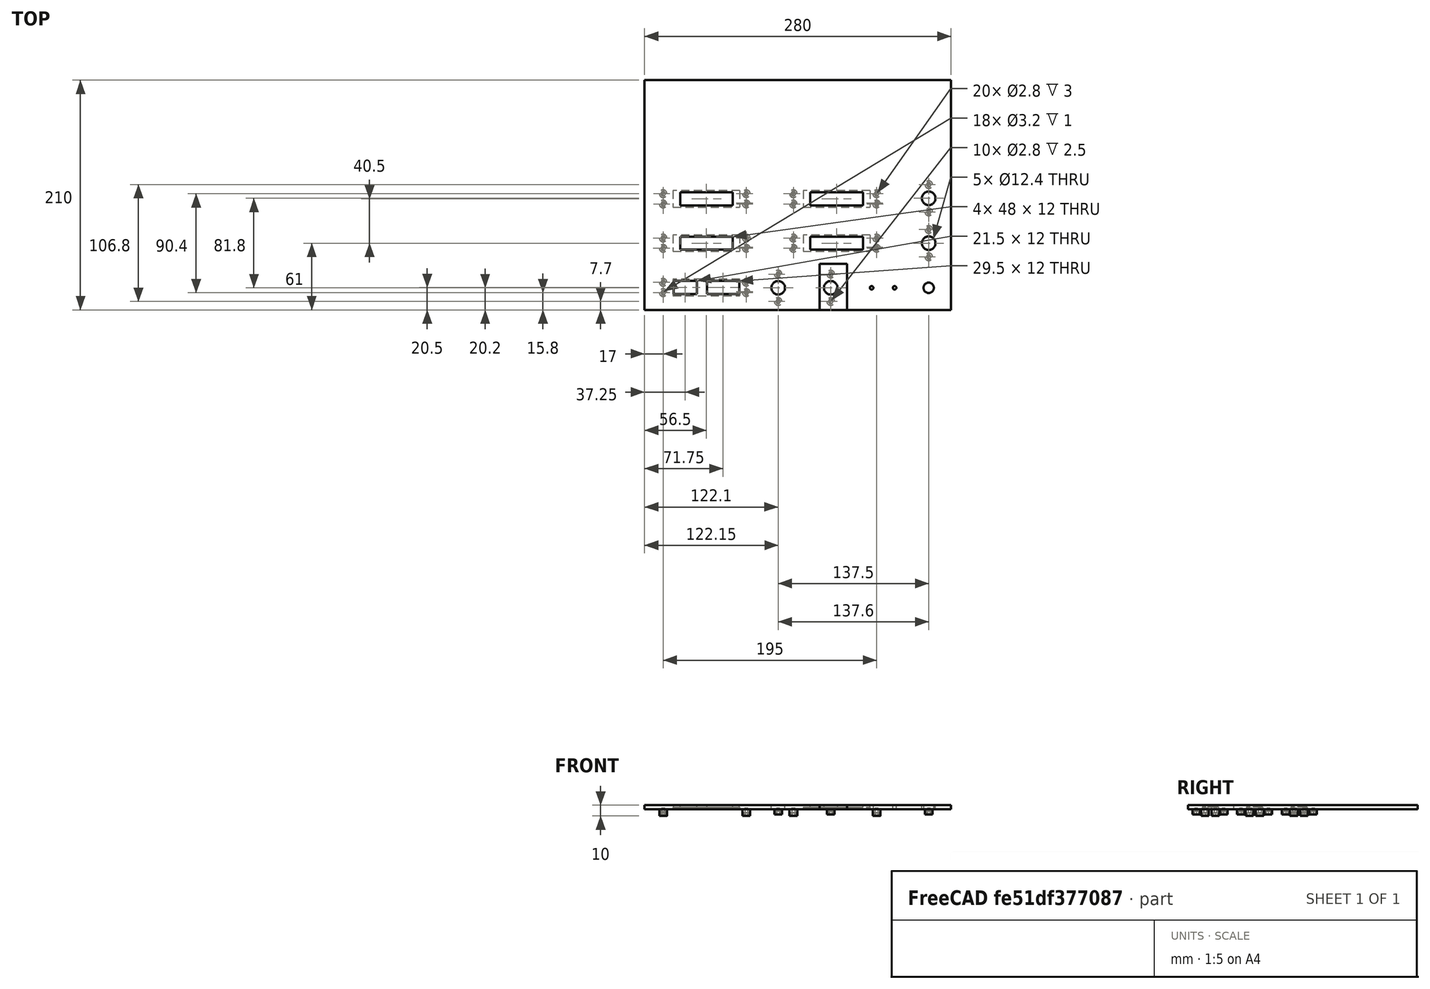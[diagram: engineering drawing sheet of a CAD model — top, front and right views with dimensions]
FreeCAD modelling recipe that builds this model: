
FCSTD DOCUMENT  (FreeCAD 0.17R13522 (Git))
Label: test_panel_para_encoder_doble
License: CreativeCommons Attribution-ShareAlike
LicenseURL: http://creativecommons.org/licenses/by-sa/4.0/
objects: Part::Feature×69, Part::Fuse×58, Part::Cut×20, Part::Box×8, Part::Part2DObjectPython×8, Part::FeaturePython×4, App::DocumentObjectGroup×2, Part::Extrusion×1
note: 168 computed .brp shape members not serialized (recipe doc carries the construction recipe); baked Part::Feature solids carry a one-line shape summary decoded from their .brp

FEATURE [Part::Box] Box  label="base principal"
  AttacherType = Attacher::AttachEngine3D
  Height = 4
  Length = 280
  Placement = pos=(0,0,-4) rot=(0,0,1;0rad)
  Width = 210
FEATURE [Part::Feature] Fusion008001001  label="perforador encoder"
  Placement = pos=(17,17,-6) rot=(1,0,0;3.14159rad)
  shape: bbox 82.5 x 15 x 10 mm, 18 faces (baked)
FEATURE [Part::Feature] Fusion008001001001  label="perforador active 1"
  Placement = pos=(17,98,-6) rot=(1,0,0;3.14159rad)
  shape: bbox 82.5 x 15 x 10 mm, 18 faces (baked)
FEATURE [Part::Feature] Fusion008001001002  label="perforador active 2"
  Placement = pos=(17,57.5,-6) rot=(1,0,0;3.14159rad)
  shape: bbox 82.5 x 15 x 10 mm, 18 faces (baked)
FEATURE [Part::Feature] Fusion008001001003  label="perforador standby 1"
  Placement = pos=(136,98,-6) rot=(1,0,0;3.14159rad)
  shape: bbox 82.5 x 15 x 10 mm, 18 faces (baked)
FEATURE [Part::Feature] Fusion008001001004  label="perforador standby 2"
  Placement = pos=(136,57.5,-6) rot=(1,0,0;3.14159rad)
  shape: bbox 82.5 x 15 x 10 mm, 18 faces (baked)
FEATURE [Part::Cut] Cut
  Base = -> Box
  Refine = true
  Tool = -> Fusion008001001
FEATURE [Part::Cut] Cut001
  Base = -> Cut
  Refine = true
  Tool = -> Fusion008001001001
FEATURE [Part::Cut] Cut002
  Base = -> Cut001
  Refine = true
  Tool = -> Fusion008001001002
FEATURE [Part::Cut] Cut003
  Base = -> Cut002
  Refine = true
  Tool = -> Fusion008001001003
FEATURE [Part::Cut] Cut004  label="base con 7 segmentos sin frente perforado"
  Base = -> Cut003
  Refine = true
  Tool = -> Fusion008001001004
FEATURE [Part::Feature] BooleanFragments001  label="perforador encoder izquierda"
  Placement = pos=(130,20.2,4) rot=(0,0,1;0rad)
  shape: bbox 45.2 x 30 x 10 mm, 34 faces, 4 solids (baked)
FEATURE [Part::Feature] BooleanFragments002  label="perforador encoder derecha"
  Placement = pos=(178,20.2,4) rot=(0,0,1;0rad)
  shape: bbox 45.2 x 30 x 10 mm, 34 faces, 4 solids (baked)
FEATURE [Part::Cut] Cut005
  Base = -> Cut004
  Refine = true
  Tool = -> BooleanFragments001
FEATURE [Part::Cut] Cut006  label="frente con agujeros displays y encoders transponder"
  Base = -> Cut005
  Refine = true
  Tool = -> BooleanFragments002
FEATURE [Part::Feature] Fusion005001  label="boton ident"
  Placement = pos=(203,14.2,1) rot=(0,0,1;0rad)
  shape: bbox 30 x 12 x 10 mm, 14 faces (baked)
FEATURE [Part::Cut] Cut007
  Base = -> Cut006
  Refine = true
  Tool = -> Fusion005001
FEATURE [Part::Part2DObjectPython] Line009  # Draft 2D object (typed FeaturePython)
  ChamferSize = 0
  Closed = false
  End = (270.847,20.2,0)
  FilletRadius = 0
  Length = 35.3471
  MakeFace = false
  Points = (2) [(235.5,20.2,0),(270.847,20.2,0)]
  Start = (235.5,20.2,0)
  Subdivisions = 0
FEATURE [Part::Part2DObjectPython] Circle  # Draft 2D object (typed FeaturePython)
  FirstAngle = 0
  LastAngle = 0
  MakeFace = false
  Placement = pos=(269.619,20.2,4) rot=(0,0,1;0rad)
  Radius = 4.75
FEATURE [Part::Part2DObjectPython] Circle001  # Draft 2D object (typed FeaturePython)
  FirstAngle = 0
  LastAngle = 0
  MakeFace = false
  Placement = pos=(259.67,20.2,0) rot=(0,0,1;0rad)
  Radius = 14
FEATURE [Part::Extrusion] Extrude
  Base = -> Circle
  Dir = (0,0,1)
  DirMode = 2
  FaceMakerClass = Part::FaceMakerBullseye
  LengthFwd = 10
  LengthRev = 0
  Placement = pos=(-10,0,-10) rot=(0,0,1;0rad)
  Solid = true
  Symmetric = false
FEATURE [Part::Part2DObjectPython] Line014  # Draft 2D object (typed FeaturePython)
  ChamferSize = 0
  Closed = false
  End = (248.272,28.2144,0)
  FilletRadius = 0
  Length = 13.696
  MakeFace = false
  Placement = pos=(-10,0,-4) rot=(0,0,1;0rad)
  Points = (2) [(269.378,20.2,4),(258.272,28.2144,4)]
  Start = (259.378,20.2,0)
  Subdivisions = 0
FEATURE [Part::Part2DObjectPython] Line015  # Draft 2D object (typed FeaturePython)
  ChamferSize = 0
  Closed = false
  End = (254.876,33.263,0)
  FilletRadius = 0
  Length = 13.7518
  MakeFace = false
  Placement = pos=(-10,0,-4) rot=(0,0,1;0rad)
  Points = (2) [(269.174,20.2,4),(264.876,33.263,4)]
  Start = (259.174,20.2,0)
  Subdivisions = 0
FEATURE [Part::Part2DObjectPython] Line016  # Draft 2D object (typed FeaturePython)
  ChamferSize = 0
  Closed = false
  End = (263.227,33.6931,0)
  FilletRadius = 0
  Length = 14.1488
  MakeFace = false
  Placement = pos=(-10,0,-4) rot=(0,0,1;0rad)
  Points = (2) [(268.97,20.2,4),(273.227,33.6931,4)]
  Start = (258.97,20.2,0)
  Subdivisions = 0
FEATURE [Part::Part2DObjectPython] Line017  # Draft 2D object (typed FeaturePython)
  ChamferSize = 0
  Closed = false
  End = (270.612,28.9289,0)
  FilletRadius = 0
  Length = 14.5511
  MakeFace = false
  Placement = pos=(-10,0,-4) rot=(0,0,1;0rad)
  Points = (2) [(268.97,20.2,4),(280.612,28.9289,4)]
  Start = (258.97,20.2,0)
  Subdivisions = 0
FEATURE [Part::Part2DObjectPython] Line  # Draft 2D object (typed FeaturePython)
  ChamferSize = 0
  Closed = true
  End = (269.619,20.2,0)
  FilletRadius = 0
  Length = 0
  MakeFace = false
  Points = (2) [(269.619,20.2,0),(269.619,20.2,0)]
  Start = (269.619,20.2,0)
  Subdivisions = 0
FEATURE [App::DocumentObjectGroup] Construction
  Group = -> [Line009,Circle001,Line014,Line015,Line016,Line017,Line]
FEATURE [Part::Cut] Cut008  label="base con line inferior completa"
  Base = -> Cut007
  Refine = true
  Tool = -> Extrude
FEATURE [Part::Feature] BooleanFragments003  label="perforador para comunication 1"
  Placement = pos=(251.8,102,3) rot=(0,0,1;3.14159rad)
  shape: bbox 45.2 x 30 x 10 mm, 34 faces, 4 solids (baked)
FEATURE [Part::Feature] BooleanFragments003001  label="perforador para comunication 2"
  Placement = pos=(251.8,61,4) rot=(0,0,1;3.14159rad)
  shape: bbox 45.2 x 30 x 10 mm, 34 faces, 4 solids (baked)
FEATURE [Part::Cut] Cut009
  Base = -> Cut008
  Refine = true
  Tool = -> BooleanFragments003001
FEATURE [Part::Cut] Cut010  label="panel sin botones y sin leds"
  Base = -> Cut009
  Refine = true
  Tool = -> BooleanFragments003
FEATURE [Part::Feature] Cut001001  label="the_spacer_1mm_inside"
  Placement = pos=(17,106.2,0) rot=(0.99953,0.030644,0;3.14159rad)
  shape: bbox 7 x 7 x 6 mm, 11 faces (baked)
FEATURE [Part::Fuse] Fusion
  Base = -> Cut010
  Refine = true
  Tool = -> Cut001001
FEATURE [Part::Box] Box001  label="Cube"
  AttacherType = Attacher::AttachEngine3D
  Height = 3
  Length = 6
  Placement = pos=(14,103,-3) rot=(0,0,1;0rad)
  Width = 6
FEATURE [Part::Fuse] Fusion008001001005
  Base = -> Fusion
  Refine = true
  Tool = -> Box001
FEATURE [Part::Feature] Cut001001001  label="the_spacer_1mm_inside001"
  Placement = pos=(17,96.8,0) rot=(0.99953,0.030644,0;3.14159rad)
  shape: bbox 7 x 7 x 6 mm, 11 faces (baked)
FEATURE [Part::Feature] Box001001  label="Cube001"
  Placement = pos=(14,94,-3) rot=(0,0,1;0rad)
  shape: bbox 6 x 6 x 3 mm, 6 faces (baked)
FEATURE [Part::Fuse] Fusion008001001006
  Base = -> Fusion008001001005
  Refine = true
  Tool = -> Cut001001001
FEATURE [Part::Fuse] Fusion008001001007
  Base = -> Box001001
  Placement = pos=(0,0,1) rot=(0,0,1;0rad)
  Refine = true
  Tool = -> Fusion008001001006
FEATURE [Part::Feature] Cut001001001001  label="the_spacer_1mm_inside002"
  Placement = pos=(17,56.3,0) rot=(0.99953,0.030644,0;3.14159rad)
  shape: bbox 7 x 7 x 6 mm, 11 faces (baked)
FEATURE [Part::Feature] Cut001001001002  label="the_spacer_1mm_inside003"
  Placement = pos=(17,65.7,0) rot=(0.99953,0.030644,0;3.14159rad)
  shape: bbox 7 x 7 x 6 mm, 11 faces (baked)
FEATURE [Part::Feature] Cut001001001002001  label="the_spacer_1mm_inside004"
  Placement = pos=(17,25.2,0) rot=(0.99953,0.030644,0;3.14159rad)
  shape: bbox 7 x 7 x 6 mm, 11 faces (baked)
FEATURE [Part::Feature] Cut001001001001001  label="the_spacer_1mm_inside005"
  Placement = pos=(17,15.8,0) rot=(0.99953,0.030644,0;3.14159rad)
  shape: bbox 7 x 7 x 6 mm, 11 faces (baked)
FEATURE [Part::Feature] Cut001001001002002  label="the_spacer_1mm_inside006"
  Placement = pos=(136,106.2,0) rot=(0.99953,0.030644,0;3.14159rad)
  shape: bbox 7 x 7 x 6 mm, 11 faces (baked)
FEATURE [Part::Feature] Cut001001001002003  label="the_spacer_1mm_inside007"
  Placement = pos=(136,96.8,0) rot=(0.99953,0.030644,0;3.14159rad)
  shape: bbox 7 x 7 x 6 mm, 11 faces (baked)
FEATURE [Part::Feature] Cut001001001002004  label="the_spacer_1mm_inside008"
  Placement = pos=(136,65.7,0) rot=(0.99953,0.030644,0;3.14159rad)
  shape: bbox 7 x 7 x 6 mm, 11 faces (baked)
FEATURE [Part::Feature] Cut001001001001002  label="the_spacer_1mm_inside009"
  Placement = pos=(136,56.3,0) rot=(0.99953,0.030644,0;3.14159rad)
  shape: bbox 7 x 7 x 6 mm, 11 faces (baked)
FEATURE [Part::Feature] Cut001001001001002001  label="the_spacer_1mm_inside010"
  Placement = pos=(93,65.7,0) rot=(0.99953,0.030644,0;3.14159rad)
  shape: bbox 7 x 7 x 6 mm, 11 faces (baked)
FEATURE [Part::Feature] Cut001001001002002001  label="the_spacer_1mm_inside011"
  Placement = pos=(93,106.2,0) rot=(0.99953,0.030644,0;3.14159rad)
  shape: bbox 7 x 7 x 6 mm, 11 faces (baked)
FEATURE [Part::Feature] Cut001001001002003001  label="the_spacer_1mm_inside012"
  Placement = pos=(93,96.8,0) rot=(0.99953,0.030644,0;3.14159rad)
  shape: bbox 7 x 7 x 6 mm, 11 faces (baked)
FEATURE [Part::Feature] Cut001001001001002002  label="the_spacer_1mm_inside013"
  Placement = pos=(93,56.3,0) rot=(0.99953,0.030644,0;3.14159rad)
  shape: bbox 7 x 7 x 6 mm, 11 faces (baked)
FEATURE [Part::Feature] Cut001001001002001001  label="the_spacer_1mm_inside014"
  Placement = pos=(93,25.2,0) rot=(0.99953,0.030644,0;3.14159rad)
  shape: bbox 7 x 7 x 6 mm, 11 faces (baked)
FEATURE [Part::Feature] Cut001001001001001001  label="the_spacer_1mm_inside015"
  Placement = pos=(93,15.8,0) rot=(0.99953,0.030644,0;3.14159rad)
  shape: bbox 7 x 7 x 6 mm, 11 faces (baked)
FEATURE [Part::Feature] Cut001001001002002001001  label="the_spacer_1mm_inside016"
  Placement = pos=(212,106.2,0) rot=(0.99953,0.030644,0;3.14159rad)
  shape: bbox 7 x 7 x 6 mm, 11 faces (baked)
FEATURE [Part::Feature] Cut001001001002003001001  label="the_spacer_1mm_inside017"
  Placement = pos=(212,96.8,0) rot=(0.99953,0.030644,0;3.14159rad)
  shape: bbox 7 x 7 x 6 mm, 11 faces (baked)
FEATURE [Part::Feature] Cut001001001001002001001  label="the_spacer_1mm_inside018"
  Placement = pos=(212,65.7,0) rot=(0.99953,0.030644,0;3.14159rad)
  shape: bbox 7 x 7 x 6 mm, 11 faces (baked)
FEATURE [Part::Feature] Cut001001001001002002001  label="the_spacer_1mm_inside019"
  Placement = pos=(212,56.3,0) rot=(0.99953,0.030644,0;3.14159rad)
  shape: bbox 7 x 7 x 6 mm, 11 faces (baked)
FEATURE [Part::Fuse] Fusion008001001008
  Base = -> Cut001001001001
  Refine = true
  Tool = -> Cut001001001002
FEATURE [Part::Fuse] Fusion008001001009
  Base = -> Cut001001001002001
  Refine = true
  Tool = -> Cut001001001001001
FEATURE [Part::Fuse] Fusion008001001010
  Base = -> Cut001001001002002001
  Refine = true
  Tool = -> Cut001001001002003001
FEATURE [Part::Fuse] Fusion008001001011
  Base = -> Cut001001001002002001
  Refine = true
  Tool = -> Cut001001001002003001
FEATURE [Part::Fuse] Fusion008001001012
  Base = -> Cut001001001001002001
  Refine = true
  Tool = -> Cut001001001001002002
FEATURE [Part::Fuse] Fusion008001001013
  Base = -> Cut001001001002001001
  Refine = true
  Tool = -> Cut001001001001001001
FEATURE [Part::Fuse] Fusion008001001014
  Base = -> Cut001001001002002
  Refine = true
  Tool = -> Cut001001001002003
FEATURE [Part::Fuse] Fusion008001001015
  Base = -> Cut001001001002002
  Refine = true
  Tool = -> Cut001001001002003
FEATURE [Part::Fuse] Fusion008001001016
  Base = -> Cut001001001002004
  Refine = true
  Tool = -> Cut001001001001002
FEATURE [Part::Fuse] Fusion008001001017
  Base = -> Cut001001001002002001001
  Refine = true
  Tool = -> Cut001001001002003001001
FEATURE [Part::Fuse] Fusion008001001018
  Base = -> Cut001001001001002001001
  Refine = true
  Tool = -> Cut001001001001002002001
FEATURE [Part::FeaturePython] BooleanFragments  # WARN: FeaturePython — macro-defined, semantics opaque (R4)
  Mode = 0
  Objects = -> [Fusion008001001007,Fusion008001001008]
  Tolerance = 0
FEATURE [Part::FeaturePython] BooleanFragments003002  # WARN: FeaturePython — macro-defined, semantics opaque (R4)
  Mode = 0
  Objects = -> [BooleanFragments,Fusion008001001009]
  Tolerance = 0
FEATURE [Part::FeaturePython] BooleanFragments003003  # WARN: FeaturePython — macro-defined, semantics opaque (R4)
  Mode = 0
  Objects = -> [BooleanFragments003002,Fusion008001001010]
  Tolerance = 0
FEATURE [Part::FeaturePython] BooleanFragments003004  # WARN: FeaturePython — macro-defined, semantics opaque (R4)
  Mode = 0
  Objects = -> [BooleanFragments003003,Fusion008001001012]
  Tolerance = 0
FEATURE [Part::Fuse] Fusion008001001019
  Base = -> Fusion008001001013
  Refine = true
  Tool = -> BooleanFragments003004
FEATURE [Part::Fuse] Fusion008001001020
  Base = -> Fusion008001001014
  Refine = true
  Tool = -> Fusion008001001019
FEATURE [Part::Fuse] Fusion008001001021
  Base = -> Fusion008001001014
  Refine = true
  Tool = -> Fusion008001001019
FEATURE [Part::Fuse] Fusion008001001022
  Base = -> Fusion008001001011
  Refine = true
  Tool = -> Fusion008001001020
FEATURE [Part::Fuse] Fusion008001001023
  Base = -> Fusion008001001021
  Refine = true
  Tool = -> Fusion008001001022
FEATURE [Part::Fuse] Fusion008001001024
  Base = -> Fusion008001001016
  Refine = true
  Tool = -> Fusion008001001023
FEATURE [Part::Fuse] Fusion008001001025
  Base = -> Fusion008001001017
  Refine = true
  Tool = -> Fusion008001001024
FEATURE [Part::Fuse] Fusion008001001026
  Base = -> Fusion008001001018
  Refine = true
  Tool = -> Fusion008001001025
FEATURE [Part::Fuse] Fusion008001001027
  Base = -> Fusion008001001015
  Refine = true
  Tool = -> Fusion008001001026
FEATURE [Part::Feature] Box001001001  label="Cube002"
  Placement = pos=(14,53.5,-2) rot=(0,0,1;0rad)
  shape: bbox 6 x 6 x 3 mm, 6 faces (baked)
FEATURE [Part::Feature] Box001001002  label="Cube003"
  Placement = pos=(14,62.5,-2) rot=(0,0,1;0rad)
  shape: bbox 6 x 6 x 3 mm, 6 faces (baked)
FEATURE [Part::Feature] Box001001001001  label="Cube004"
  Placement = pos=(14,13,-2) rot=(0,0,1;0rad)
  shape: bbox 6 x 6 x 3 mm, 6 faces (baked)
FEATURE [Part::Feature] Box001001002001  label="Cube005"
  Placement = pos=(14,22,-2) rot=(0,0,1;0rad)
  shape: bbox 6 x 6 x 3 mm, 6 faces (baked)
FEATURE [Part::Feature] Box001001002002  label="Cube006"
  Placement = pos=(133,62.5,-2) rot=(0,0,1;0rad)
  shape: bbox 6 x 6 x 3 mm, 6 faces (baked)
FEATURE [Part::Feature] Box001001001002  label="Cube007"
  Placement = pos=(133,53.5,-2) rot=(0,0,1;0rad)
  shape: bbox 6 x 6 x 3 mm, 6 faces (baked)
FEATURE [Part::Feature] Box001001002002001  label="Cube008"
  Placement = pos=(133,103,-2) rot=(0,0,1;0rad)
  shape: bbox 6 x 6 x 3 mm, 6 faces (baked)
FEATURE [Part::Feature] Box001001001002001  label="Cube009"
  Placement = pos=(133,94,-2) rot=(0,0,1;0rad)
  shape: bbox 6 x 6 x 3 mm, 6 faces (baked)
FEATURE [Part::Fuse] Fusion008001001028
  Base = -> Fusion008001001027
  Refine = true
  Tool = -> Box001001001001
FEATURE [Part::Fuse] Fusion008001001029
  Base = -> Box001001002001
  Refine = true
  Tool = -> Fusion008001001028
FEATURE [Part::Fuse] Fusion008001001030
  Base = -> Box001001001002001
  Refine = true
  Tool = -> Fusion008001001029
FEATURE [Part::Fuse] Fusion008001001031
  Base = -> Box001001002002001
  Refine = true
  Tool = -> Fusion008001001030
FEATURE [Part::Feature] Box001001001002002  label="Cube010"
  Placement = pos=(90,53.5,-2) rot=(0,0,1;0rad)
  shape: bbox 6 x 6 x 3 mm, 6 faces (baked)
FEATURE [Part::Feature] Box001001002002002  label="Cube011"
  Placement = pos=(90,62.5,-2) rot=(0,0,1;0rad)
  shape: bbox 6 x 6 x 3 mm, 6 faces (baked)
FEATURE [Part::Feature] Box001001001002003  label="Cube012"
  Placement = pos=(209,54.5,-2) rot=(0,0,1;0rad)
  shape: bbox 6 x 6 x 3 mm, 6 faces (baked)
FEATURE [Part::Feature] Box001001002002002001  label="Cube013"
  Placement = pos=(209,62.5,-2) rot=(0,0,1;0rad)
  shape: bbox 6 x 6 x 3 mm, 6 faces (baked)
FEATURE [Part::Feature] Box001001001002002001  label="Cube014"
  Placement = pos=(90,13.5,-2) rot=(0,0,1;0rad)
  shape: bbox 6 x 6 x 3 mm, 6 faces (baked)
FEATURE [Part::Feature] Box001001002002002002  label="Cube015"
  Placement = pos=(90,22.5,-2) rot=(0,0,1;0rad)
  shape: bbox 6 x 6 x 3 mm, 6 faces (baked)
FEATURE [Part::Fuse] Fusion008001001032
  Base = -> Fusion008001001031
  Refine = true
  Tool = -> Box001001002002002002
FEATURE [Part::Fuse] Fusion008001001033
  Base = -> Box001001001002002001
  Refine = true
  Tool = -> Fusion008001001032
FEATURE [Part::Fuse] Fusion008001001034
  Base = -> Box001001001
  Refine = true
  Tool = -> Fusion008001001033
FEATURE [Part::Fuse] Fusion008001001035
  Base = -> Box001001002
  Refine = true
  Tool = -> Fusion008001001034
FEATURE [Part::Fuse] Fusion008001001036
  Base = -> Box001001001002
  Refine = true
  Tool = -> Fusion008001001035
FEATURE [Part::Fuse] Fusion008001001037
  Base = -> Box001001002002
  Refine = true
  Tool = -> Fusion008001001036
FEATURE [Part::Feature] Box001001002002002001001  label="Cube016"
  Placement = pos=(209,103.5,-2) rot=(0,0,1;0rad)
  shape: bbox 6 x 6 x 3 mm, 6 faces (baked)
FEATURE [Part::Fuse] Fusion008001001038
  Base = -> Box001001002002002001
  Refine = true
  Tool = -> Fusion008001001037
FEATURE [Part::Feature] Box001001001002003001  label="Cube017"
  Placement = pos=(209,94.5,-2) rot=(0,0,1;0rad)
  shape: bbox 6 x 6 x 3 mm, 6 faces (baked)
FEATURE [Part::Fuse] Fusion008001001039
  Base = -> Box001001001002003
  Refine = true
  Tool = -> Fusion008001001038
FEATURE [Part::Fuse] Fusion008001001040
  Base = -> Box001001001002003001
  Refine = true
  Tool = -> Fusion008001001039
FEATURE [Part::Fuse] Fusion008001001041
  Base = -> Box001001002002002001001
  Refine = true
  Tool = -> Fusion008001001040
FEATURE [Part::Feature] Box001001001002002002  label="Cube018"
  Placement = pos=(90,94.5,-2) rot=(0,0,1;0rad)
  shape: bbox 6 x 6 x 3 mm, 6 faces (baked)
FEATURE [Part::Fuse] Fusion008001001042
  Base = -> Box001001001002002
  Refine = true
  Tool = -> Fusion008001001041
FEATURE [Part::Fuse] Fusion008001001043
  Base = -> Box001001001002002002
  Refine = true
  Tool = -> Fusion008001001042
FEATURE [Part::Feature] Box001001002002002001002  label="Cube019"
  Placement = pos=(90,103.5,-2) rot=(0,0,1;0rad)
  shape: bbox 6 x 6 x 3 mm, 6 faces (baked)
FEATURE [Part::Fuse] Fusion008001001044
  Base = -> Box001001002002002
  Refine = true
  Tool = -> Fusion008001001043
FEATURE [Part::Fuse] Fusion008001001045
  Base = -> Box001001002002002001002
  Refine = true
  Tool = -> Fusion008001001044
FEATURE [Part::Box] Box001001002002002001003  label="Cube020"
  AttacherType = Attacher::AttachEngine3D
  Height = 20
  Length = 48
  Placement = pos=(32.5,55,-5) rot=(0,0,1;0rad)
  Width = 12
FEATURE [Part::Feature] Box001001002002002001003001  label="Cube021"
  Placement = pos=(32.5,95.5,-5) rot=(0,0,1;0rad)
  shape: bbox 48 x 12 x 20 mm, 6 faces (baked)
FEATURE [Part::Feature] Box001001002002002001003001001  label="Cube022"
  Placement = pos=(151.5,95.5,-5) rot=(0,0,1;0rad)
  shape: bbox 48 x 12 x 20 mm, 6 faces (baked)
FEATURE [Part::Feature] Box001001002002002001003001001001  label="Cube023"
  Placement = pos=(151.5,55,-5) rot=(0,0,1;0rad)
  shape: bbox 48 x 12 x 20 mm, 6 faces (baked)
FEATURE [Part::Cut] Cut001001001002003001002
  Base = -> Fusion008001001045
  Refine = true
  Tool = -> Box001001002002002001003001001001
FEATURE [Part::Cut] Cut001001001002003001003
  Base = -> Cut001001001002003001002
  Refine = true
  Tool = -> Box001001002002002001003001001
FEATURE [Part::Cut] Cut001001001002003001004
  Base = -> Cut001001001002003001003
  Refine = true
  Tool = -> Box001001002002002001003001
FEATURE [Part::Cut] Cut001001001002003001005
  Base = -> Cut001001001002003001004
  Refine = true
  Tool = -> Box001001002002002001003
FEATURE [Part::Box] Box001001002002002001003001001002  label="Cube024"
  AttacherType = Attacher::AttachEngine3D
  Height = 30
  Length = 21.5
  Placement = pos=(26.5,14.5,-12) rot=(0,0,1;0rad)
  Width = 12
FEATURE [Part::Box] Box001001002002002001003001001003  label="Cube025"
  AttacherType = Attacher::AttachEngine3D
  Height = 30
  Length = 29.5
  Placement = pos=(57,14.5,-12) rot=(0,0,1;0rad)
  Width = 12
FEATURE [Part::Cut] Cut001001001002003001006
  Base = -> Cut001001001002003001005
  Refine = true
  Tool = -> Box001001002002002001003001001002
FEATURE [Part::Cut] Cut001001001002003001007  label="panel con 5 displayes y sus spacers"
  Base = -> Cut001001001002003001006
  Refine = true
  Tool = -> Box001001002002002001003001001003
FEATURE [Part::Feature] Cut001001001002003001008  label="the_spacer_1.5_mm_inside"
  Placement = pos=(170.1,7.7,1.5) rot=(0.999812,0.019404,0;3.14159rad)
  shape: bbox 7 x 7 x 6 mm, 11 faces (baked)
FEATURE [Part::Feature] Cut001001001002003001008001  label="the_spacer_1.5_mm_inside001"
  Placement = pos=(122.1,7.7,1.5) rot=(0.999812,0.019404,0;3.14159rad)
  shape: bbox 7 x 7 x 6 mm, 11 faces (baked)
FEATURE [Part::Feature] Cut001001001002003001008002  label="the_spacer_1.5_mm_inside002"
  Placement = pos=(170.1,32.7,1.5) rot=(0.999812,0.019404,0;3.14159rad)
  shape: bbox 7 x 7 x 6 mm, 11 faces (baked)
FEATURE [Part::Feature] Cut001001001002003001008002001  label="the_spacer_1.5_mm_inside003"
  Placement = pos=(122.1,32.7,1.5) rot=(0.999812,0.019404,0;3.14159rad)
  shape: bbox 7 x 7 x 6 mm, 11 faces (baked)
FEATURE [Part::Feature] Cut001001001002003001008002002  label="the_spacer_1.5_mm_inside004"
  Placement = pos=(259.7,48.5,1.5) rot=(0.999812,0.019404,0;3.14159rad)
  shape: bbox 7 x 7 x 6 mm, 11 faces (baked)
FEATURE [Part::Feature] Cut001001001002003001008002002001  label="the_spacer_1.5_mm_inside005"
  Placement = pos=(259.7,73.5,1.5) rot=(0.999812,0.019404,0;3.14159rad)
  shape: bbox 7 x 7 x 6 mm, 11 faces (baked)
FEATURE [Part::Feature] Cut001001001002003001008002002002  label="the_spacer_1.5_mm_inside006"
  Placement = pos=(259.7,89.5,1.5) rot=(0.999812,0.019404,0;3.14159rad)
  shape: bbox 7 x 7 x 6 mm, 11 faces (baked)
FEATURE [Part::Feature] Cut001001001002003001008002002003  label="the_spacer_1.5_mm_inside007"
  Placement = pos=(259.7,114.5,1.5) rot=(0.999812,0.019404,0;3.14159rad)
  shape: bbox 7 x 7 x 6 mm, 11 faces (baked)
FEATURE [Part::Fuse] Fusion008001001046
  Base = -> Cut001001001002003001007
  Refine = true
  Tool = -> Cut001001001002003001008
FEATURE [Part::Fuse] Fusion008001001047
  Base = -> Cut001001001002003001008001
  Refine = true
  Tool = -> Fusion008001001046
FEATURE [Part::Fuse] Fusion008001001048
  Base = -> Cut001001001002003001008002
  Refine = true
  Tool = -> Fusion008001001047
FEATURE [Part::Fuse] Fusion008001001049
  Base = -> Cut001001001002003001008002001
  Refine = true
  Tool = -> Fusion008001001048
FEATURE [Part::Fuse] Fusion008001001050
  Base = -> Cut001001001002003001008002002
  Refine = true
  Tool = -> Fusion008001001049
FEATURE [Part::Fuse] Fusion008001001051
  Base = -> Cut001001001002003001008002002001
  Refine = true
  Tool = -> Fusion008001001050
FEATURE [Part::Fuse] Fusion008001001052
  Base = -> Cut001001001002003001008002002002
  Refine = true
  Tool = -> Fusion008001001051
FEATURE [Part::Fuse] Fusion008001001053
  Base = -> Cut001001001002003001008002002003
  Refine = true
  Tool = -> Fusion008001001052
FEATURE [Part::Feature] Box001001002002002001003001001004  label="Cube026"
  Placement = pos=(257,45.5,-2) rot=(0,0,1;0rad)
  shape: bbox 6 x 6 x 3 mm, 6 faces (baked)
FEATURE [Part::Feature] Box001001002002002001003001001004001  label="Cube027"
  Placement = pos=(257,70.5,-2) rot=(0,0,1;0rad)
  shape: bbox 6 x 6 x 3 mm, 6 faces (baked)
FEATURE [Part::Fuse] Fusion008001001054
  Base = -> Fusion008001001053
  Refine = true
  Tool = -> Box001001002002002001003001001004
FEATURE [Part::Feature] Box001001002002002001003001001004001001  label="Cube028"
  Placement = pos=(257,86.5,-2) rot=(0,0,1;0rad)
  shape: bbox 6 x 6 x 3 mm, 6 faces (baked)
FEATURE [Part::Fuse] Fusion008001001055
  Base = -> Box001001002002002001003001001004001
  Refine = true
  Tool = -> Fusion008001001054
FEATURE [Part::Feature] Box001001002002002001003001001004001001001  label="Cube029"
  Placement = pos=(257,111.5,-2) rot=(0,0,1;0rad)
  shape: bbox 6 x 6 x 3 mm, 6 faces (baked)
FEATURE [Part::Fuse] Fusion008001001056
  Base = -> Box001001002002002001003001001004001001
  Refine = true
  Tool = -> Fusion008001001055
FEATURE [Part::Feature] Box001001002002002001003001001004001001001001  label="Cube030"
  Placement = pos=(167,5,-2) rot=(0,0,1;0rad)
  shape: bbox 6 x 6 x 3 mm, 6 faces (baked)
FEATURE [Part::Fuse] Fusion008001001057
  Base = -> Box001001002002002001003001001004001001001
  Refine = true
  Tool = -> Fusion008001001056
FEATURE [Part::Feature] Box001001002002002001003001001004001001001001001  label="Cube031"
  Placement = pos=(119,5,-2) rot=(0,0,1;0rad)
  shape: bbox 6 x 6 x 3 mm, 6 faces (baked)
FEATURE [Part::Fuse] Fusion008001001058
  Base = -> Box001001002002002001003001001004001001001001
  Refine = true
  Tool = -> Fusion008001001057
FEATURE [Part::Feature] Box001001002002002001003001001004001001001001001001  label="Cube032"
  Placement = pos=(119,30,-2) rot=(0,0,1;0rad)
  shape: bbox 6 x 6 x 3 mm, 6 faces (baked)
FEATURE [Part::Fuse] Fusion008001001059
  Base = -> Box001001002002002001003001001004001001001001001
  Refine = true
  Tool = -> Fusion008001001058
FEATURE [Part::Feature] Box001001002002002001003001001004001001001001001001001  label="Cube033"
  Placement = pos=(167,30,-2) rot=(0,0,1;0rad)
  shape: bbox 6 x 6 x 3 mm, 6 faces (baked)
FEATURE [Part::Fuse] Fusion008001001060
  Base = -> Box001001002002002001003001001004001001001001001001
  Refine = true
  Tool = -> Fusion008001001059
FEATURE [Part::Fuse] Fusion008001001061
  Base = -> Box001001002002002001003001001004001001001001001001001
  Refine = true
  Tool = -> Fusion008001001060
FEATURE [App::DocumentObjectGroup] Group  label="spacers para encoders dobles"
  Group = -> [Fusion008001001061]
FEATURE [Part::Feature] Fusion008001001061001  label="panel_siplays_encoders_dobles_y_spacers"
  shape: bbox 280 x 210 x 10 mm, 411 faces (baked)
FEATURE [Part::Box] Box001001002002002001003001001004001001001001001001002  label="Cube034"
  AttacherType = Attacher::AttachEngine3D
  Height = 30
  Length = 200
  Placement = pos=(-40,-22,-10) rot=(0,0,1;0rad)
  Width = 2800
FEATURE [Part::Cut] Cut001001001002003001008002002004
  Base = -> Fusion008001001061001
  Refine = true
  Tool = -> Box001001002002002001003001001004001001001001001001002
FEATURE [Part::Box] Box001001002002002001003001001004001001001001001001003  label="Cube035"
  AttacherType = Attacher::AttachEngine3D
  Height = 60
  Length = 100
  Placement = pos=(185,-18,-12) rot=(0,0,1;0rad)
  Width = 300
FEATURE [Part::Cut] Cut001001001002003001008002002005
  Base = -> Cut001001001002003001008002002004
  Refine = true
  Tool = -> Box001001002002002001003001001004001001001001001001003
FEATURE [Part::Box] Box001001002002002001003001001004001001001001001001004  label="Cube036"
  AttacherType = Attacher::AttachEngine3D
  Height = 80
  Length = 100
  Placement = pos=(99,42,-23) rot=(0,0,1;0rad)
  Width = 300
FEATURE [Part::Cut] Cut001001001002003001008002002006
  Base = -> Cut001001001002003001008002002005
  Refine = true
  Tool = -> Box001001002002002001003001001004001001001001001001004
